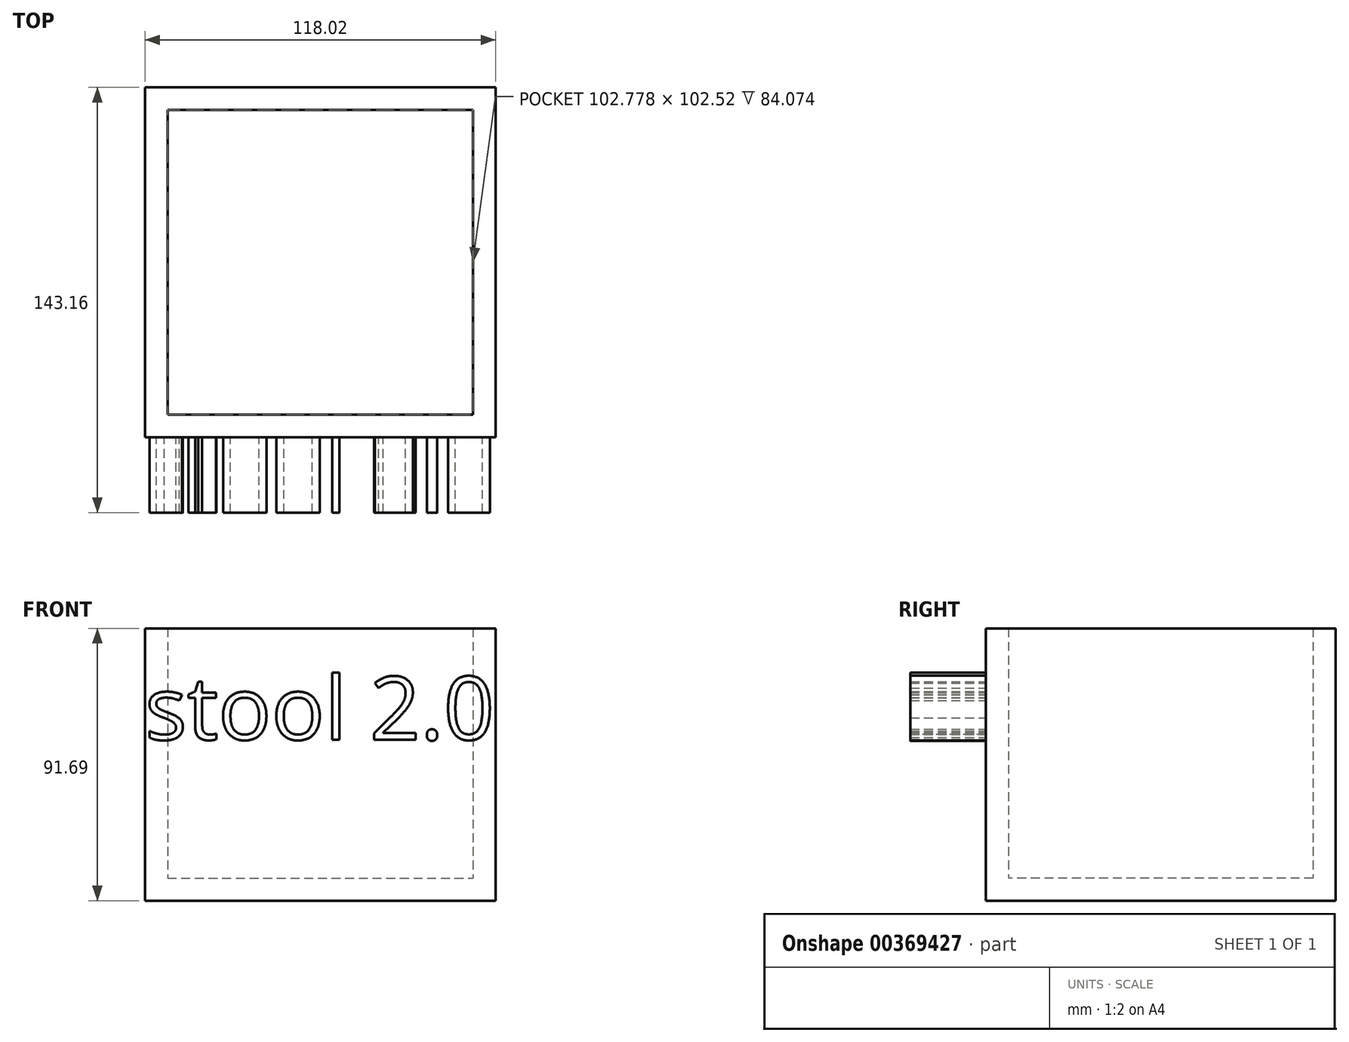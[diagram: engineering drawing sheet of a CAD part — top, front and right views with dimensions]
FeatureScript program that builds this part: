
annotation { "Feature Type Name" : "Feature", "Feature Type Description" : "" }
export const myFeature = defineFeature(function(context is Context, id is Id, definition is map)
    precondition{}
    {
        {
            var Q0;
            Q0=qCreatedBy(makeId("Top.planeOp"),FACE);
            var sketch = newSketch(context, id + "F0", { "sketchPlane" : qUnion([Q0])});
            skLineSegment(sketch, "E0.bottom", {"start": v(-42, 41.1) * mm, "end": v(76.02, 41.1) * mm});
            skLineSegment(sketch, "E0.top", {"start": v(-42, -76.66) * mm, "end": v(76.02, -76.66) * mm});
            skLineSegment(sketch, "E0.left", {"start": v(-42, 41.1) * mm, "end": v(-42, -76.66) * mm});
            skLineSegment(sketch, "E0.right", {"start": v(76.02, 41.1) * mm, "end": v(76.02, -76.66) * mm});
            skSolve(sketch);
        }
        {
            var Q0;
            Q0 = qSketchRegion(id + "F0", true);
            extrude(context, id + "F1", {"entities" : qUnion([Q0]), "depth" : 91.7 * mm});
        }
        {
            var Q0;
            Q0=makeQuery(id+"F1.opExtrude","SWEPT_FACE",FACE,{"disambiguationData":[OSD([sQuery(id+"F0.wireOp",EDGE,"E0.top")])]});
            var sketch = newSketch(context, id + "F2", { "sketchPlane" : qUnion([Q0])});
            skText(sketch, "E1", { "text": "stool 2.0\n", "fontName": "OpenSans-Regular.ttf"});
            const initialGuessF2  = {"E1": [-0.042, 0.05421, 1, 0, 0.02137]};
            skSetInitialGuess(sketch, initialGuessF2);
            skSolve(sketch);
        }
        {
            var Q0;
            Q0=makeQuery(id+"F1.opExtrude","CAP_FACE",FACE,{"disambiguationData":[OSD([sQuery(id+"F0.wireOp",EDGE,"E0.bottom"),sQuery(id+"F0.wireOp",EDGE,"E0.top"),sQuery(id+"F0.wireOp",EDGE,"E0.left"),sQuery(id+"F0.wireOp",EDGE,"E0.right")])],"isStart":false});
            shell(context, id + "F3", {"entities" : qUnion([Q0]), "thickness" : 7.62 * mm});
        }
        {
            var Q0;
            Q0 = qSketchRegion(id + "F2", true);
            extrude(context, id + "F4", {"entities" : qUnion([Q0]), "operationType" : NewBodyOperationType.ADD, "depth" : 25.4 * mm});
        }
    });
